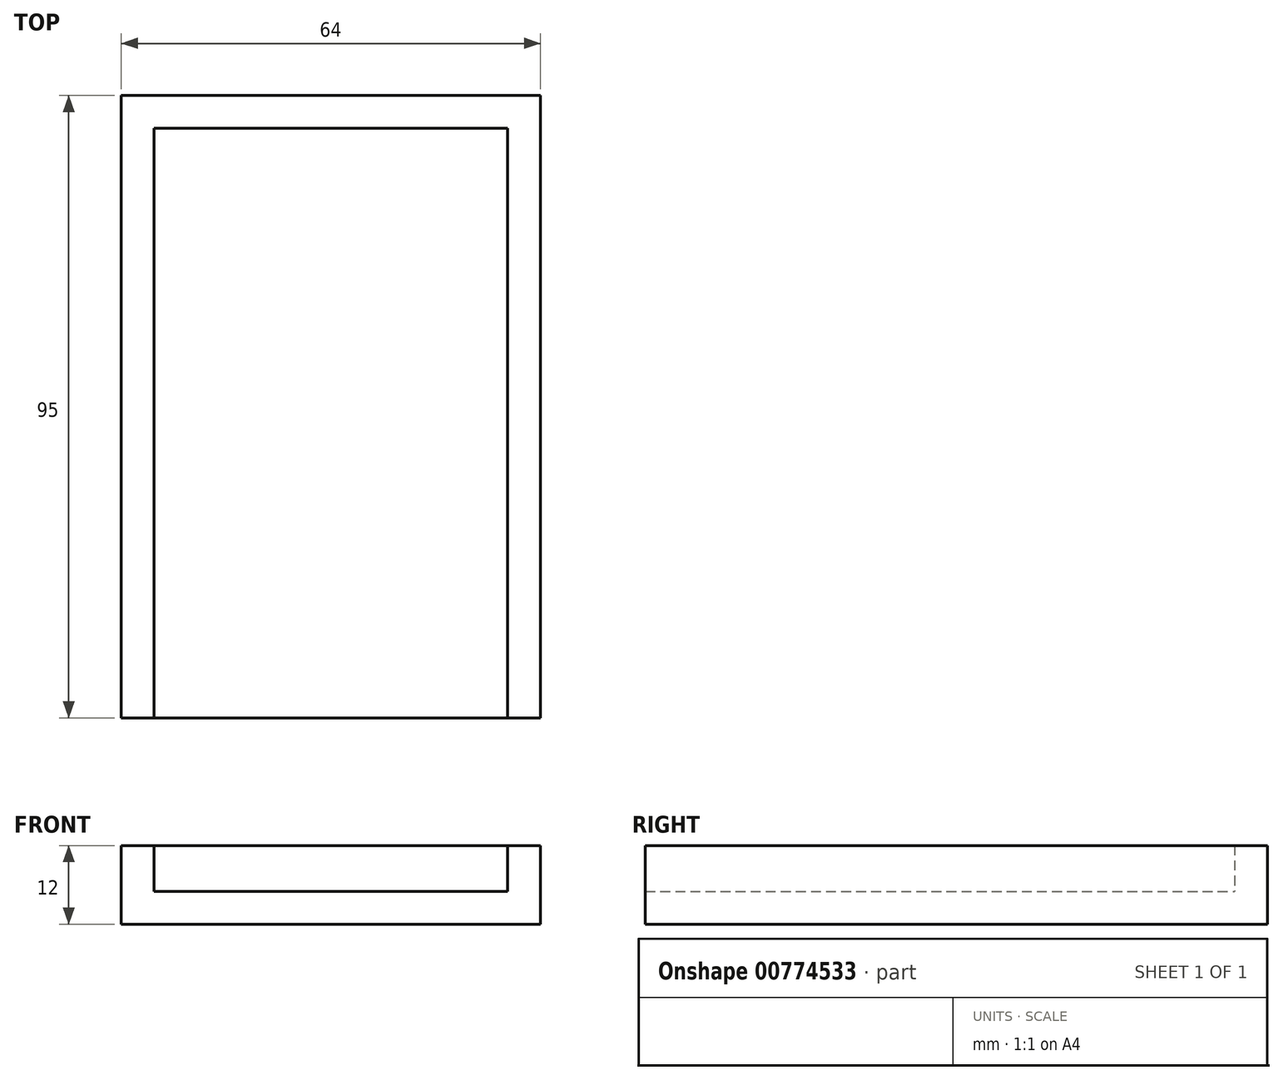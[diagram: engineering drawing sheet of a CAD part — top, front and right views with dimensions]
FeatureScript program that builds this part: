
annotation { "Feature Type Name" : "Feature", "Feature Type Description" : "" }
export const myFeature = defineFeature(function(context is Context, id is Id, definition is map)
    precondition{}
    {
        {
            var Q0;
            Q0=qCreatedBy(makeId("Front.planeOp"),FACE);
            var sketch = newSketch(context, id + "F0", { "sketchPlane" : qUnion([Q0])});
            skLineSegment(sketch, "E0.bottom", {"start": v(-32, 12) * mm, "end": v(-27, 12) * mm});
            skLineSegment(sketch, "E0.left", {"start": v(-32, 12) * mm, "end": v(-32, 0) * mm});
            skLineSegment(sketch, "E0.right", {"start": v(-27, 12) * mm, "end": v(-27, 5) * mm});
            skLineSegment(sketch, "E1.bottom", {"start": v(-32, 0) * mm, "end": v(0, 0) * mm});
            skLineSegment(sketch, "E2", {"start": v(-27, 5) * mm, "end": v(0, 5) * mm});
            skLineSegment(sketch, "E3.MirrorCS", {"start": v(32, 12) * mm, "end": v(27, 12) * mm});
            skLineSegment(sketch, "E4.MirrorCS", {"start": v(32, 12) * mm, "end": v(32, 0) * mm});
            skLineSegment(sketch, "E5.MirrorCS", {"start": v(32, 0) * mm, "end": v(0, 0) * mm});
            skLineSegment(sketch, "E6.MirrorCS", {"start": v(27, 5) * mm, "end": v(0, 5) * mm});
            skLineSegment(sketch, "E7.MirrorCS", {"start": v(27, 12) * mm, "end": v(27, 5) * mm});
            skLineSegment(sketch, "E8", {"start": v(-27, 12) * mm, "end": v(27, 12) * mm});
            skSolve(sketch);
        }
        {
            var Q0;
            Q0=makeQuery(id+"F0.imprint","IMPRINT",FACE,{"disambiguationData":[TD([[makeQuery(id+"F0.imprint","IMPRINT",EDGE,{"derivedFrom":sQuery(id+"F0.wireOp",EDGE,"E0.bottom")}),-1.0]])]});
            extrude(context, id + "F1", {"entities" : qUnion([Q0]), "depth" : 90 * mm, "offsetDistance" : 25 * mm});
        }
        {
            var Q0;
            Q0 = qSketchRegion(id + "F0", true);
            extrude(context, id + "F2", {"entities" : qUnion([Q0]), "operationType" : NewBodyOperationType.ADD, "oppositeDirection" : true, "depth" : 5 * mm, "offsetDistance" : 25 * mm});
        }
    });
